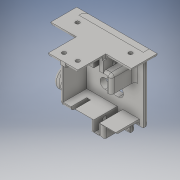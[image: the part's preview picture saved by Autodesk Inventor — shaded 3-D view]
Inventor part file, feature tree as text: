
AUTODESK INVENTOR PART (.ipt)
format: ipt  version: 2016 (Build 200138000, 138)  size: 712,192 bytes
history: native  units: in
note: dims shown in document units (in); Inventor stores cm internally (conversion verified against a paired STEP export)
features: sketch x17, extrude x15, fillet x7, hole x2, plane x1, rib x1
ambient origin geometry x8: Origin, YZ Plane, XZ Plane, XY Plane, X Axis, Y Axis, Z Axis, Center Point
bodies: Solid1 (feature_tree)
feature tree (43):
  extrude  "Extrusion1"  Depth=0.8976in
  sketch  "Sketch12"  dims[d11=0.0787in d12=0.0787in d13=0.0787in d14=0.0787in d82=0.9016in d83=0.8858in]
  extrude  "Extrusion7"  Depth=0.9016in
  extrude  "Extrusion13"  Depth=0.1102in
  extrude  "Extrusion14"  Depth=0.6142in
  extrude  "Extrusion15"  Depth=0.1614in
  fillet  "Fillet23"  Radius=0.2992in
  extrude  "Extrusion18"  Depth=0.2165in
  extrude  "Extrusion20"  Depth=0.0787in
  extrude  "Extrusion21"  Depth=0.0787in
  extrude  "Extrusion22"  Depth=0.0787in
  extrude  "Extrusion23"  Depth=0.0787in
  extrude  "Extrusion24"  Depth=0.0394in
  extrude  "Extrusion25"  Depth=0.0394in
  hole  "Hole6"  [1 undecoded]
  plane  "Work Plane7"
  rib  "Rib1"
  hole  "Hole7"  [1 undecoded]
  fillet  "Fillet46"  Radius=0.9016in
  fillet  "Fillet47"  Radius=0.1378in
  extrude  "Extrusion26"  Depth=0.3543in
  fillet  "Fillet48"  Radius=0.2165in
  extrude  "Extrusion27"  Depth=0.3937in TaperAngle=0.0deg
  extrude  "Extrusion28"  Depth=0.0787in
  fillet  "Fillet49"  Radius=0.1772in
  fillet  "Fillet50"  Radius=0.0483in
  fillet  "Fillet51"  Radius=0.1063in
  sketch  "Sketch1"  dims[d2=0.1181in d3=0.0in d6=0.8976in d9=0.357in d10=0.7139in]
  sketch  "Sketch22"  dims[d85=0.1102in d86=0.1102in]
  sketch  "Sketch32"  dims[d87=0.6142in d88=0.6142in]
  sketch  "Sketch35"  dims[d89=0.1614in d90=0.1614in d91=0.2992in]
  sketch  "Sketch36"  dims[d92=0.2165in d93=0.2165in]
  sketch  "Sketch41"  dims[d95=0.9016in d97=0.0787in]
  sketch  "Sketch43"  dims[d98=0.0787in d100=0.0787in]
  sketch  "Sketch46"  dims[d101=0.0787in d102=0.0787in]
  sketch  "Sketch47"  dims[d103=0.1693in d105=0.0787in]
  sketch  "Sketch48"  dims[d106=0.0394in d107=0.0394in]
  sketch  "Sketch49"  dims[d108=0.0394in d109=0.0394in]
  sketch  "Sketch50"  dims[d110=0.1575in d111=0.0787in]
  sketch  "Sketch51"  dims[d112=0.0787in d113=0.0394in d114=0.9016in d125=0.1378in]
  sketch  "Sketch52"  dims[d130=0.185in d132=0.3543in d133=0.2165in]
  sketch  "Sketch53"  dims[d139=0.0394in d164=0.3937in d165=0.0in]
  sketch  "Sketch54"  dims[d181=0.0787in d182=0.0787in d185=0.1772in d186=0.0483in d187=0.1063in d190=0.3135in d191=0.4724in d192=0.0in d205=0.1575in d206=0.0in d207=0.0394in d208=0.3937in d209=0.0in d214=0.0591in d252=0.0197in d253=0.0in d267=0.1969in d268=0.1969in d269=0.1575in d270=0.1575in d271=0.3937in d272=0.0in d276=0.4016in d277=0.0in d278=0.4724in d279=0.0in d280=0.1614in d281=0.0in d282=0.1614in d283=0.0in d284=0.5906in d285=0.5118in d286=0.562in d287=0.0in d288=0.2598in d289=0.2598in d290=0.2756in d291=0.2756in d292=0.1575in d293=0.1575in d294=0.1575in d295=0.1575in d296=0.0787in d297=0.2362in d298=0.1575in d299=0.0787in d300=90.0deg d301=0.1575in d302=0.8108in d303=0.0394in d304=0.0984in d305=0.0in d306=0.0in d307=0.0394in d308=0.0394in d309=0.2559in d310=0.0394in d311=0.2559in d312=0.0394in d313=0.0787in d314=0.2362in d315=0.1575in d316=0.0787in d317=90.0deg d318=0.4724in d319=0.8108in d321=0.0787in d322=0.0591in d323=0.3937in d324=0.0in d325=0.0591in d326=0.2717in d327=0.2323in d328=0.2835in d329=0.4016in d330=0.1575in d331=0.0in d332=0.1575in d333=0.0in d334=0.0591in d335=0.0591in d336=0.0591in d26=0.0394in d27=0.0394in d147=0.0394in d148=0.0394in]
note: 2 required parameter values undecoded (feature->parameter linkage not recoverable at this tier; creation-order binding heuristic only, values carry confidence <= 0.55)
